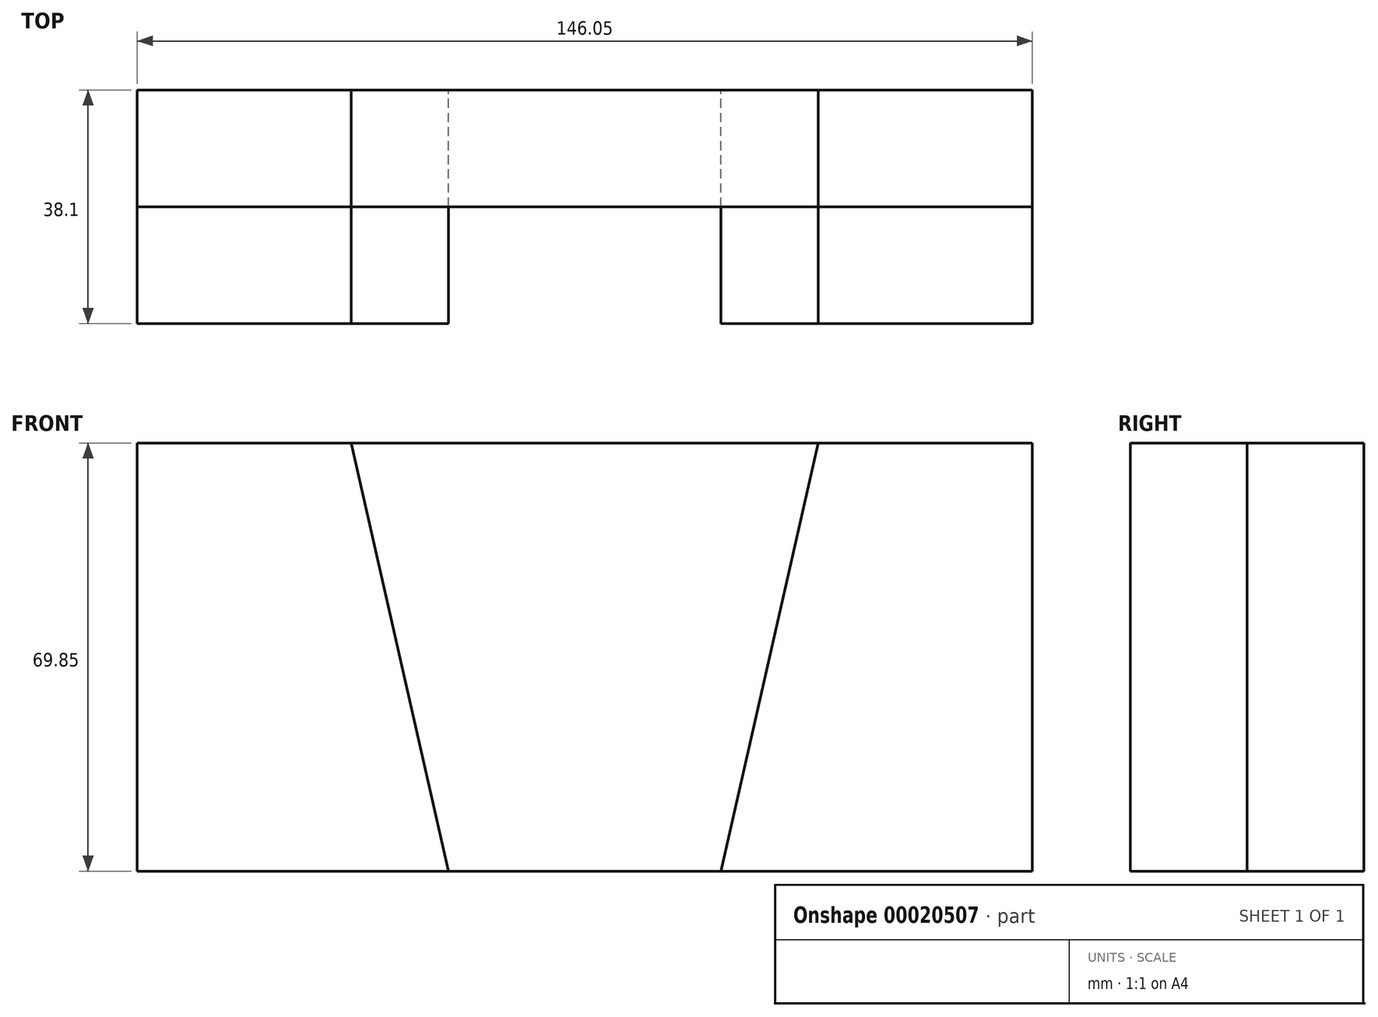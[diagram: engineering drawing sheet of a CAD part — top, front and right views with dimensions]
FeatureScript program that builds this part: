
annotation { "Feature Type Name" : "Feature", "Feature Type Description" : "" }
export const myFeature = defineFeature(function(context is Context, id is Id, definition is map)
    precondition{}
    {
        {
            var Q0;
            Q0=qCreatedBy(makeId("Front.planeOp"),FACE);
            var sketch = newSketch(context, id + "F0", { "sketchPlane" : qUnion([Q0])});
            skLineSegment(sketch, "E0.bottom", {"start": v(-59.66, 21.22) * mm, "end": v(86.4, 21.22) * mm});
            skLineSegment(sketch, "E0.top", {"start": v(-59.66, -48.63) * mm, "end": v(86.4, -48.63) * mm});
            skLineSegment(sketch, "E0.left", {"start": v(-59.66, 21.22) * mm, "end": v(-59.66, -48.63) * mm});
            skLineSegment(sketch, "E0.right", {"start": v(86.4, 21.22) * mm, "end": v(86.4, -48.63) * mm});
            skLineSegment(sketch, "E1", {"start": v(51.47, 21.22) * mm, "end": v(35.6, -48.63) * mm});
            skLineSegment(sketch, "E2", {"start": v(-24.73, 21.22) * mm, "end": v(-8.86, -48.63) * mm});
            skSolve(sketch);
        }
        {
            var Q0;
            {var subQ1=sQuery(id+"F0.wireOp",EDGE,"E0.right");Q0=makeQuery(id+"F0.imprint","IMPRINT",FACE,{"disambiguationData":[TD([[makeQuery(id+"F0.imprint","IMPRINT",EDGE,{"derivedFrom":subQ1}),-1.0]])]});}
            var Q1;
            {var subQ1=sQuery(id+"F0.wireOp",EDGE,"E0.left");Q1=makeQuery(id+"F0.imprint","IMPRINT",FACE,{"disambiguationData":[TD([[makeQuery(id+"F0.imprint","IMPRINT",EDGE,{"derivedFrom":subQ1}),1.0]])]});}
            extrude(context, id + "F1", {"entities" : qUnion([Q0, Q1]), "depth" : 38.1 * mm});
        }
        {
            var Q0;
            {var subQ1=sQuery(id+"F0.wireOp",EDGE,"E0.left");Q0=makeQuery(id+"F0.imprint","IMPRINT",FACE,{"disambiguationData":[TD([[makeQuery(id+"F0.imprint","IMPRINT",EDGE,{"derivedFrom":subQ1}),1.0]])]});}
            var Q1;
            {var subQ1=sQuery(id+"F0.wireOp",EDGE,"E0.right");Q1=makeQuery(id+"F0.imprint","IMPRINT",FACE,{"disambiguationData":[TD([[makeQuery(id+"F0.imprint","IMPRINT",EDGE,{"derivedFrom":subQ1}),-1.0]])]});}
            var Q2;
            {var subQ1=sQuery(id+"F0.wireOp",EDGE,"E1");Q2=makeQuery(id+"F0.imprint","IMPRINT",FACE,{"disambiguationData":[TD([[makeQuery(id+"F0.imprint","IMPRINT",EDGE,{"derivedFrom":subQ1}),-1.0]])]});}
            extrude(context, id + "F2", {"entities" : qUnion([Q0, Q1, Q2]), "depth" : 19.05 * mm});
        }
    });
